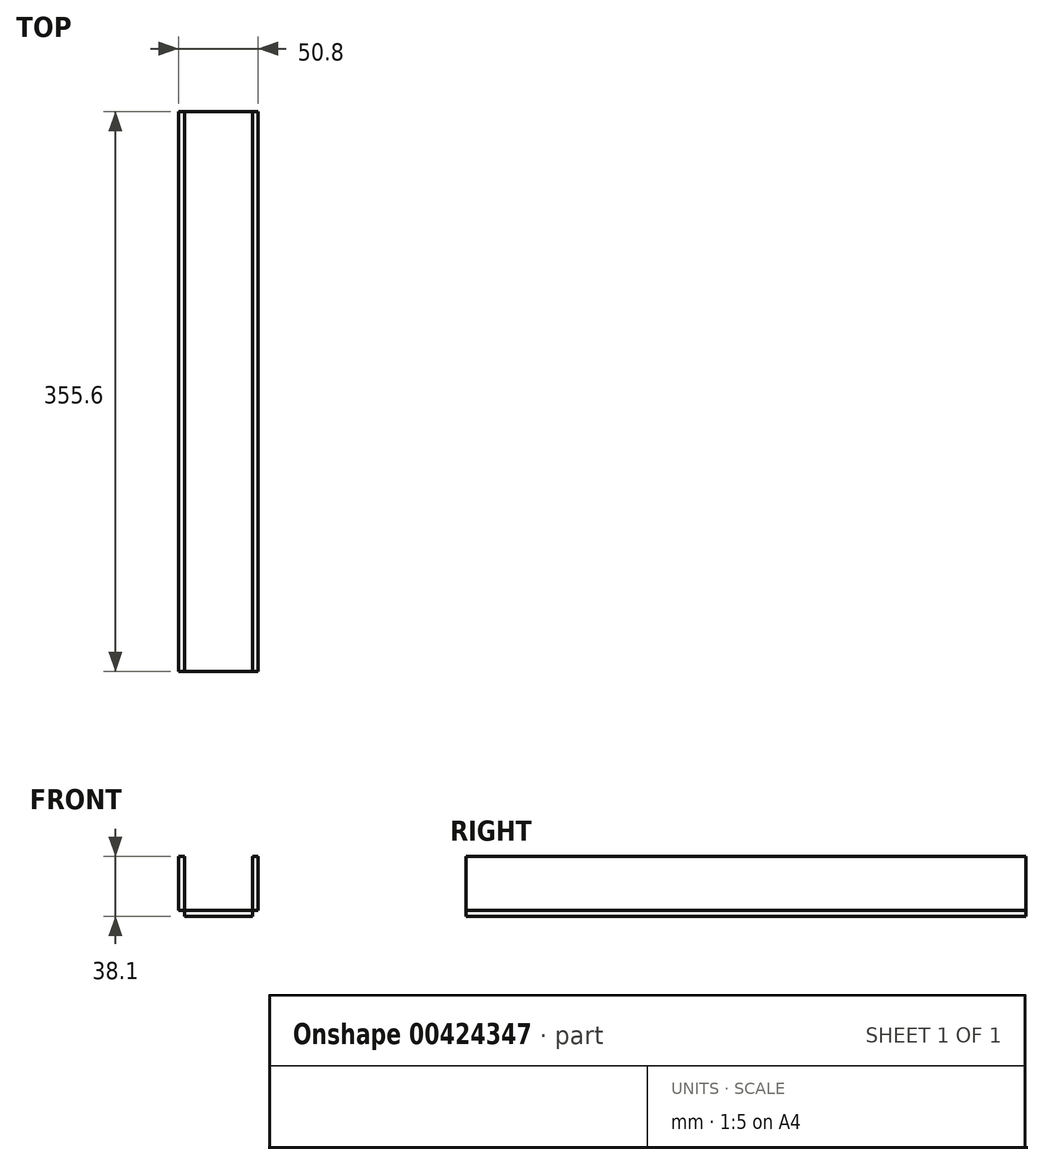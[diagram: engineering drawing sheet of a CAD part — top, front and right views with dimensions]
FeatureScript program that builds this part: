
annotation { "Feature Type Name" : "Feature", "Feature Type Description" : "" }
export const myFeature = defineFeature(function(context is Context, id is Id, definition is map)
    precondition{}
    {
        {
            var Q0;
            Q0=qCreatedBy(makeId("Front.planeOp"),FACE);
            var sketch = newSketch(context, id + "F0", { "sketchPlane" : qUnion([Q0])});
            skLineSegment(sketch, "E0.bottom", {"start": v(-56.25, 31.35) * mm, "end": v(-52.44, 31.35) * mm});
            skLineSegment(sketch, "E0.top", {"start": v(-56.25, -6.75) * mm, "end": v(-52.44, -6.75) * mm});
            skLineSegment(sketch, "E0.left", {"start": v(-56.25, 31.35) * mm, "end": v(-56.25, -6.75) * mm});
            skLineSegment(sketch, "E0.right", {"start": v(-52.44, 31.35) * mm, "end": v(-52.44, -6.75) * mm});
            skLineSegment(sketch, "E1.bottom", {"start": v(-56.25, -6.75) * mm, "end": v(-5.45, -6.75) * mm});
            skLineSegment(sketch, "E1.top", {"start": v(-56.25, -2.94) * mm, "end": v(-5.45, -2.94) * mm});
            skLineSegment(sketch, "E1.left", {"start": v(-56.25, -6.75) * mm, "end": v(-56.25, -2.94) * mm});
            skLineSegment(sketch, "E1.right", {"start": v(-5.45, -6.75) * mm, "end": v(-5.45, -2.94) * mm});
            skLineSegment(sketch, "E2.bottom", {"start": v(-5.45, -6.75) * mm, "end": v(-9.26, -6.75) * mm});
            skLineSegment(sketch, "E2.top", {"start": v(-5.45, 31.35) * mm, "end": v(-9.26, 31.35) * mm});
            skLineSegment(sketch, "E2.left", {"start": v(-5.45, -6.75) * mm, "end": v(-5.45, 31.35) * mm});
            skLineSegment(sketch, "E2.right", {"start": v(-9.26, -6.75) * mm, "end": v(-9.26, 31.35) * mm});
            skSolve(sketch);
        }
        {
            var Q0;
            {var subQ5=sQuery(id+"F0.wireOp",EDGE,"E1.left");Q0=makeQuery(id+"F0.imprint","IMPRINT",FACE,{"disambiguationData":[TD([[makeQuery(id+"F0.imprint","IMPRINT",EDGE,{"derivedFrom":subQ5}),-1.0]])]});}
            var Q1;
            {var subQ5=sQuery(id+"F0.wireOp",EDGE,"E2.bottom");Q1=makeQuery(id+"F0.imprint","IMPRINT",FACE,{"disambiguationData":[TD([[makeQuery(id+"F0.imprint","IMPRINT",EDGE,{"derivedFrom":subQ5}),-1.0]])]});}
            var Q2;
            {var subQ0=sQuery(id+"F0.wireOp",EDGE,"E0.bottom");Q2=makeQuery(id+"F0.imprint","IMPRINT",FACE,{"disambiguationData":[TD([[makeQuery(id+"F0.imprint","IMPRINT",EDGE,{"derivedFrom":subQ0}),-1.0]])]});}
            var Q3;
            {var subQ5=sQuery(id+"F0.wireOp",EDGE,"E2.top");Q3=makeQuery(id+"F0.imprint","IMPRINT",FACE,{"disambiguationData":[TD([[makeQuery(id+"F0.imprint","IMPRINT",EDGE,{"derivedFrom":subQ5}),1.0]])]});}
            var Q4;
            {var subQ0=sQuery(id+"F0.wireOp",EDGE,"E1.bottom");var subQ1=sQuery(id+"F0.wireOp",EDGE,"E0.right");var subQ2=makeQuery(id+"F0.imprint","INTERSECT",VERTEX,{"derivedFrom":[subQ1,subQ0]});Q4=makeQuery(id+"F0.imprint","IMPRINT",FACE,{"disambiguationData":[TD([[makeQuery(id+"F0.imprint","IMPRINT",EDGE,{"disambiguationData":[TD([[subQ2,1.0]])],"derivedFrom":subQ1}),1.0]])]});}
            extrude(context, id + "F1", {"entities" : qUnion([Q0, Q1, Q2, Q3, Q4]), "depth" : 355.6 * mm});
        }
    });
